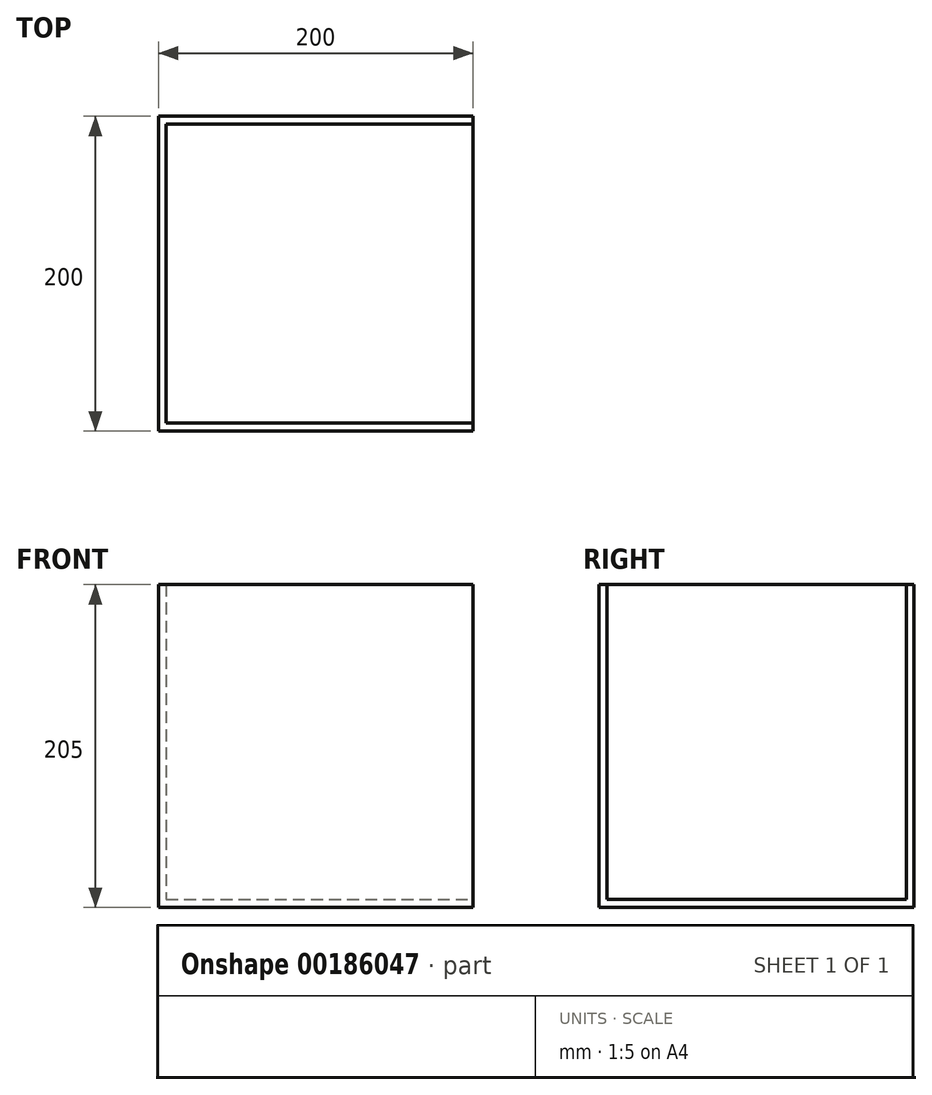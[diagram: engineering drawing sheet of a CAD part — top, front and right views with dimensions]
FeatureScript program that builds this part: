
annotation { "Feature Type Name" : "Feature", "Feature Type Description" : "" }
export const myFeature = defineFeature(function(context is Context, id is Id, definition is map)
    precondition{}
    {
        {
            var Q0;
            Q0=qCreatedBy(makeId("Top.planeOp"),FACE);
            var sketch = newSketch(context, id + "F0", { "sketchPlane" : qUnion([Q0])});
            skLineSegment(sketch, "E0.bottom", {"start": v(-100, 100) * mm, "end": v(100, 100) * mm});
            skLineSegment(sketch, "E0.top", {"start": v(-100, -100) * mm, "end": v(100, -100) * mm});
            skLineSegment(sketch, "E0.left", {"start": v(-100, 100) * mm, "end": v(-100, -100) * mm});
            skLineSegment(sketch, "E0.right", {"start": v(100, 100) * mm, "end": v(100, -100) * mm});
            skSolve(sketch);
        }
        {
            var Q0;
            Q0 = qSketchRegion(id + "F0", true);
            extrude(context, id + "F5", {"entities" : qUnion([Q0]), "oppositeDirection" : true, "depth" : 5 * mm});
        }
        {
            var Q0;
            Q0=makeQuery(id+"F5.opExtrude","SWEPT_FACE",FACE,{"disambiguationData":[OSD([sQuery(id+"F0.wireOp",EDGE,"E0.top")])]});
            var sketch = newSketch(context, id + "F1", { "sketchPlane" : qUnion([Q0])});
            skLineSegment(sketch, "E1.bottom", {"start": v(-100, 200) * mm, "end": v(100, 200) * mm});
            skLineSegment(sketch, "E1.top", {"start": v(-100, 0) * mm, "end": v(100, 0) * mm});
            skLineSegment(sketch, "E1.left", {"start": v(-100, 200) * mm, "end": v(-100, 0) * mm});
            skLineSegment(sketch, "E1.right", {"start": v(100, 200) * mm, "end": v(100, 0) * mm});
            skSolve(sketch);
        }
        {
            var Q0;
            Q0 = qSketchRegion(id + "F1", true);
            extrude(context, id + "F6", {"entities" : qUnion([Q0]), "operationType" : NewBodyOperationType.ADD, "oppositeDirection" : true, "depth" : 5 * mm});
        }
        {
            var Q0;
            Q0=makeQuery(id+"F5.opExtrude","SWEPT_FACE",FACE,{"disambiguationData":[OSD([sQuery(id+"F0.wireOp",EDGE,"E0.bottom")])]});
            var sketch = newSketch(context, id + "F2", { "sketchPlane" : qUnion([Q0])});
            skLineSegment(sketch, "E2.bottom", {"start": v(-100, 0) * mm, "end": v(100, 0) * mm});
            skLineSegment(sketch, "E2.top", {"start": v(-100, 200) * mm, "end": v(100, 200) * mm});
            skLineSegment(sketch, "E2.left", {"start": v(-100, 0) * mm, "end": v(-100, 200) * mm});
            skLineSegment(sketch, "E2.right", {"start": v(100, 0) * mm, "end": v(100, 200) * mm});
            skSolve(sketch);
        }
        {
            var Q0;
            Q0=makeQuery(id+"F2.imprint","IMPRINT",FACE,{"disambiguationData":[TD([[makeQuery(id+"F2.imprint","IMPRINT",EDGE,{"derivedFrom":sQuery(id+"F2.wireOp",EDGE,"E2.bottom")}),-1.0]])]});
            extrude(context, id + "F3", {"entities" : qUnion([Q0]), "operationType" : NewBodyOperationType.ADD, "oppositeDirection" : true, "depth" : 5 * mm});
        }
        {
            var Q0;
            Q0=makeQuery(id+"F3.boolean.opBoolean","MERGE",FACE,{"derivedFrom":[makeQuery(id+"F6.boolean.opBoolean","MERGE",FACE,{"derivedFrom":[makeQuery(id+"F5.opExtrude","SWEPT_FACE",FACE,{"disambiguationData":[OSD([sQuery(id+"F0.wireOp",EDGE,"E0.left")])]}),makeQuery(id+"F6.opExtrude","SWEPT_FACE",FACE,{"disambiguationData":[OSD([sQuery(id+"F1.wireOp",EDGE,"E1.left")])]})]}),makeQuery(id+"F3.opExtrude","SWEPT_FACE",FACE,{"disambiguationData":[OSD([sQuery(id+"F2.wireOp",EDGE,"E2.right")])]})]});
            var sketch = newSketch(context, id + "F4", { "sketchPlane" : qUnion([Q0])});
            skLineSegment(sketch, "E3.bottom", {"start": v(95, 200) * mm, "end": v(-95, 200) * mm});
            skLineSegment(sketch, "E3.top", {"start": v(95, 0) * mm, "end": v(-95, 0) * mm});
            skLineSegment(sketch, "E3.left", {"start": v(95, 200) * mm, "end": v(95, 0) * mm});
            skLineSegment(sketch, "E3.right", {"start": v(-95, 200) * mm, "end": v(-95, 0) * mm});
            skSolve(sketch);
        }
        {
            var Q0;
            Q0 = qSketchRegion(id + "F4", true);
            extrude(context, id + "F7", {"entities" : qUnion([Q0]), "operationType" : NewBodyOperationType.ADD, "oppositeDirection" : true, "depth" : 5 * mm});
        }
    });
